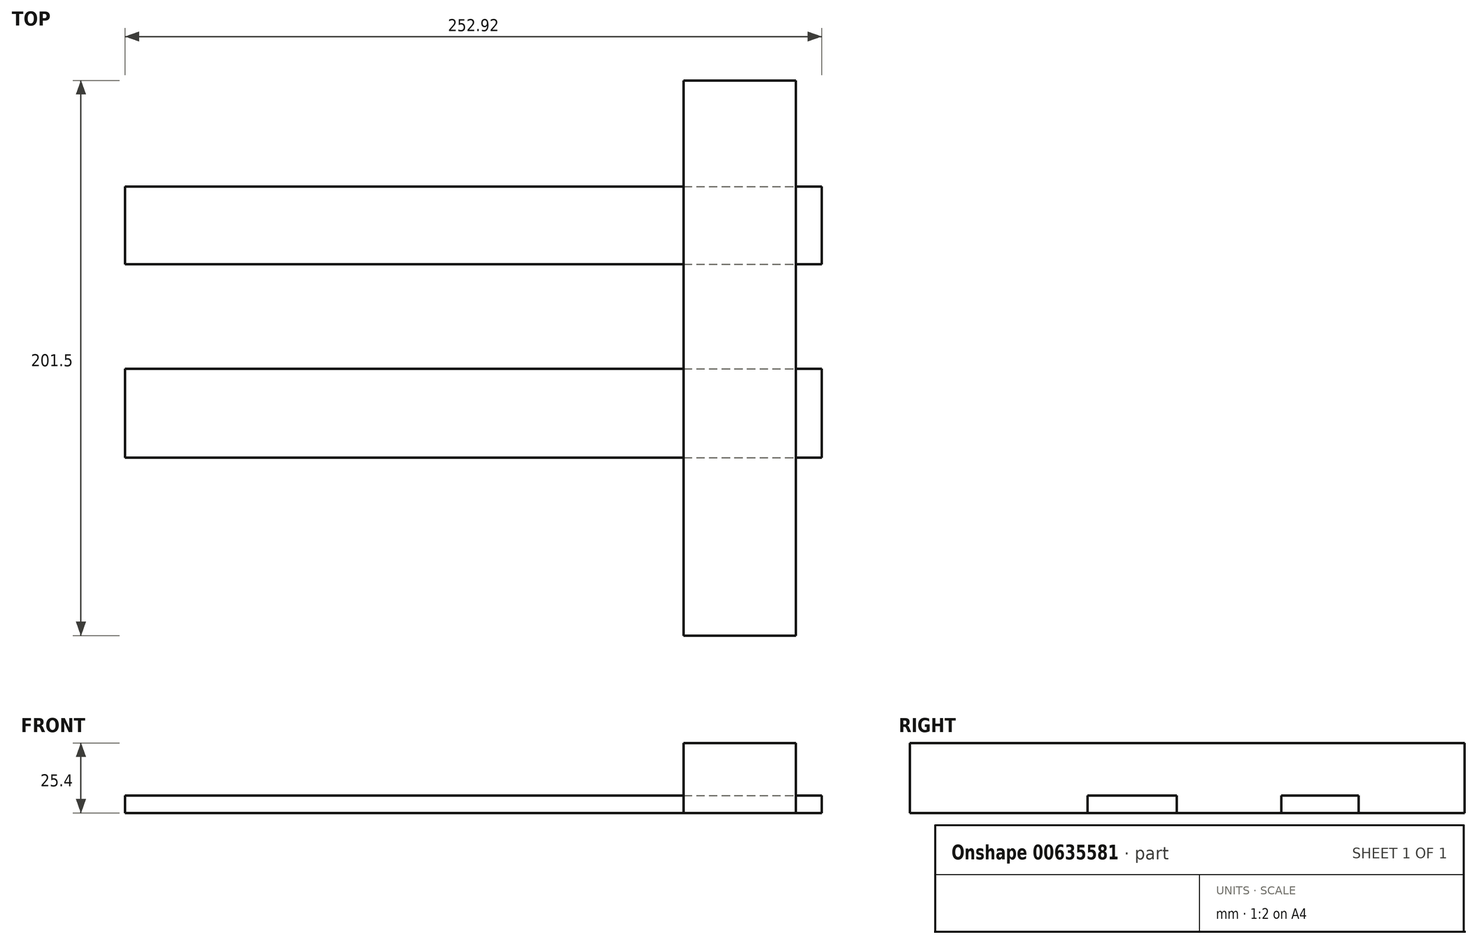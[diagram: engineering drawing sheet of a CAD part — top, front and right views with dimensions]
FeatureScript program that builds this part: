
annotation { "Feature Type Name" : "Feature", "Feature Type Description" : "" }
export const myFeature = defineFeature(function(context is Context, id is Id, definition is map)
    precondition{}
    {
        {
            var Q0;
            Q0=qCreatedBy(makeId("Top.planeOp"),FACE);
            var sketch = newSketch(context, id + "F0", { "sketchPlane" : qUnion([Q0])});
            skLineSegment(sketch, "E0.bottom", {"start": v(-136.88, 66.1) * mm, "end": v(116.04, 66.1) * mm});
            skLineSegment(sketch, "E0.top", {"start": v(-136.88, 37.98) * mm, "end": v(116.04, 37.98) * mm});
            skLineSegment(sketch, "E0.left", {"start": v(-136.88, 66.1) * mm, "end": v(-136.88, 37.98) * mm});
            skLineSegment(sketch, "E0.right", {"start": v(116.04, 66.1) * mm, "end": v(116.04, 37.98) * mm});
            skLineSegment(sketch, "E1.bottom", {"start": v(-136.88, 0) * mm, "end": v(116.04, 0) * mm});
            skLineSegment(sketch, "E1.top", {"start": v(-136.88, -32.33) * mm, "end": v(116.04, -32.33) * mm});
            skLineSegment(sketch, "E1.left", {"start": v(-136.88, 0) * mm, "end": v(-136.88, -32.33) * mm});
            skLineSegment(sketch, "E1.right", {"start": v(116.04, 0) * mm, "end": v(116.04, -32.33) * mm});
            skLineSegment(sketch, "E2.bottom", {"start": v(-81.46, 102.43) * mm, "end": v(-116.7, 102.43) * mm});
            skLineSegment(sketch, "E2.top", {"start": v(-81.46, -99.23) * mm, "end": v(-116.7, -99.23) * mm});
            skLineSegment(sketch, "E2.left", {"start": v(-81.46, 102.43) * mm, "end": v(-81.46, -99.23) * mm});
            skLineSegment(sketch, "E2.right", {"start": v(-116.7, 102.43) * mm, "end": v(-116.7, -99.23) * mm});
            skLineSegment(sketch, "E3.bottom", {"start": v(0, 105.37) * mm, "end": v(22.84, 105.37) * mm});
            skLineSegment(sketch, "E3.top", {"start": v(0, -99.98) * mm, "end": v(22.84, -99.98) * mm});
            skLineSegment(sketch, "E3.left", {"start": v(0, 105.37) * mm, "end": v(0, -99.98) * mm});
            skLineSegment(sketch, "E3.right", {"start": v(22.84, 105.37) * mm, "end": v(22.84, -99.98) * mm});
            skLineSegment(sketch, "E4.bottom", {"start": v(106.63, 104.61) * mm, "end": v(65.96, 104.61) * mm});
            skLineSegment(sketch, "E4.top", {"start": v(106.63, -96.9) * mm, "end": v(65.96, -96.9) * mm});
            skLineSegment(sketch, "E4.left", {"start": v(106.63, 104.61) * mm, "end": v(106.63, -96.9) * mm});
            skLineSegment(sketch, "E4.right", {"start": v(65.96, 104.61) * mm, "end": v(65.96, -96.9) * mm});
            skSolve(sketch);
        }
        {
            var Q0;
            Q0=makeQuery(id+"F0.imprint","IMPRINT",FACE,{"disambiguationData":[TD([[makeQuery(id+"F0.imprint","IMPRINT",EDGE,{"derivedFrom":sQuery(id+"F0.wireOp",EDGE,"E0.bottom")}),-1.0]])]});
            extrude(context, id + "F1", {"entities" : qUnion([Q0]), "depth" : 6.35 * mm, "offsetDistance" : 25.4 * mm});
        }
        {
            var Q0;
            Q0=makeQuery(id+"F0.imprint","IMPRINT",FACE,{"disambiguationData":[TD([[makeQuery(id+"F0.imprint","IMPRINT",EDGE,{"derivedFrom":sQuery(id+"F0.wireOp",EDGE,"E1.bottom")}),-1.0]])]});
            extrude(context, id + "F2", {"entities" : qUnion([Q0]), "depth" : 6.35 * mm, "offsetDistance" : 25.4 * mm});
        }
        {
            var Q0;
            {var subQ5=sQuery(id+"F0.wireOp",EDGE,"E4.top");Q0=makeQuery(id+"F0.imprint","IMPRINT",FACE,{"disambiguationData":[TD([[makeQuery(id+"F0.imprint","IMPRINT",EDGE,{"derivedFrom":subQ5}),-1.0]])]});}
            var Q1;
            {var subQ0=sQuery(id+"F0.wireOp",EDGE,"E4.left");var subQ1=sQuery(id+"F0.wireOp",EDGE,"E0.top");var subQ2=makeQuery(id+"F0.imprint","INTERSECT",VERTEX,{"derivedFrom":[subQ1,subQ0]});Q1=makeQuery(id+"F0.imprint","IMPRINT",FACE,{"disambiguationData":[TD([[makeQuery(id+"F0.imprint","IMPRINT",EDGE,{"disambiguationData":[TD([[subQ2,1.0]])],"derivedFrom":subQ1}),-1.0]])]});}
            var Q2;
            {var subQ5=sQuery(id+"F0.wireOp",EDGE,"E4.bottom");Q2=makeQuery(id+"F0.imprint","IMPRINT",FACE,{"disambiguationData":[TD([[makeQuery(id+"F0.imprint","IMPRINT",EDGE,{"derivedFrom":subQ5}),1.0]])]});}
            var Q3;
            {var subQ0=sQuery(id+"F0.wireOp",EDGE,"E4.left");var subQ1=sQuery(id+"F0.wireOp",EDGE,"E1.bottom");var subQ2=makeQuery(id+"F0.imprint","INTERSECT",VERTEX,{"derivedFrom":[subQ1,subQ0]});Q3=makeQuery(id+"F0.imprint","IMPRINT",FACE,{"disambiguationData":[TD([[makeQuery(id+"F0.imprint","IMPRINT",EDGE,{"disambiguationData":[TD([[subQ2,1.0]])],"derivedFrom":subQ1}),-1.0]])]});}
            var Q4;
            {var subQ0=sQuery(id+"F0.wireOp",EDGE,"E4.right");var subQ1=sQuery(id+"F0.wireOp",EDGE,"E0.bottom");var subQ2=makeQuery(id+"F0.imprint","INTERSECT",VERTEX,{"derivedFrom":[subQ1,subQ0]});Q4=makeQuery(id+"F0.imprint","IMPRINT",FACE,{"disambiguationData":[TD([[makeQuery(id+"F0.imprint","IMPRINT",EDGE,{"disambiguationData":[TD([[subQ2,-1.0]])],"derivedFrom":subQ1}),-1.0]])]});}
            extrude(context, id + "F3", {"entities" : qUnion([Q0, Q1, Q2, Q3, Q4]), "depth" : 25.4 * mm, "offsetDistance" : 25.4 * mm});
        }
    });
